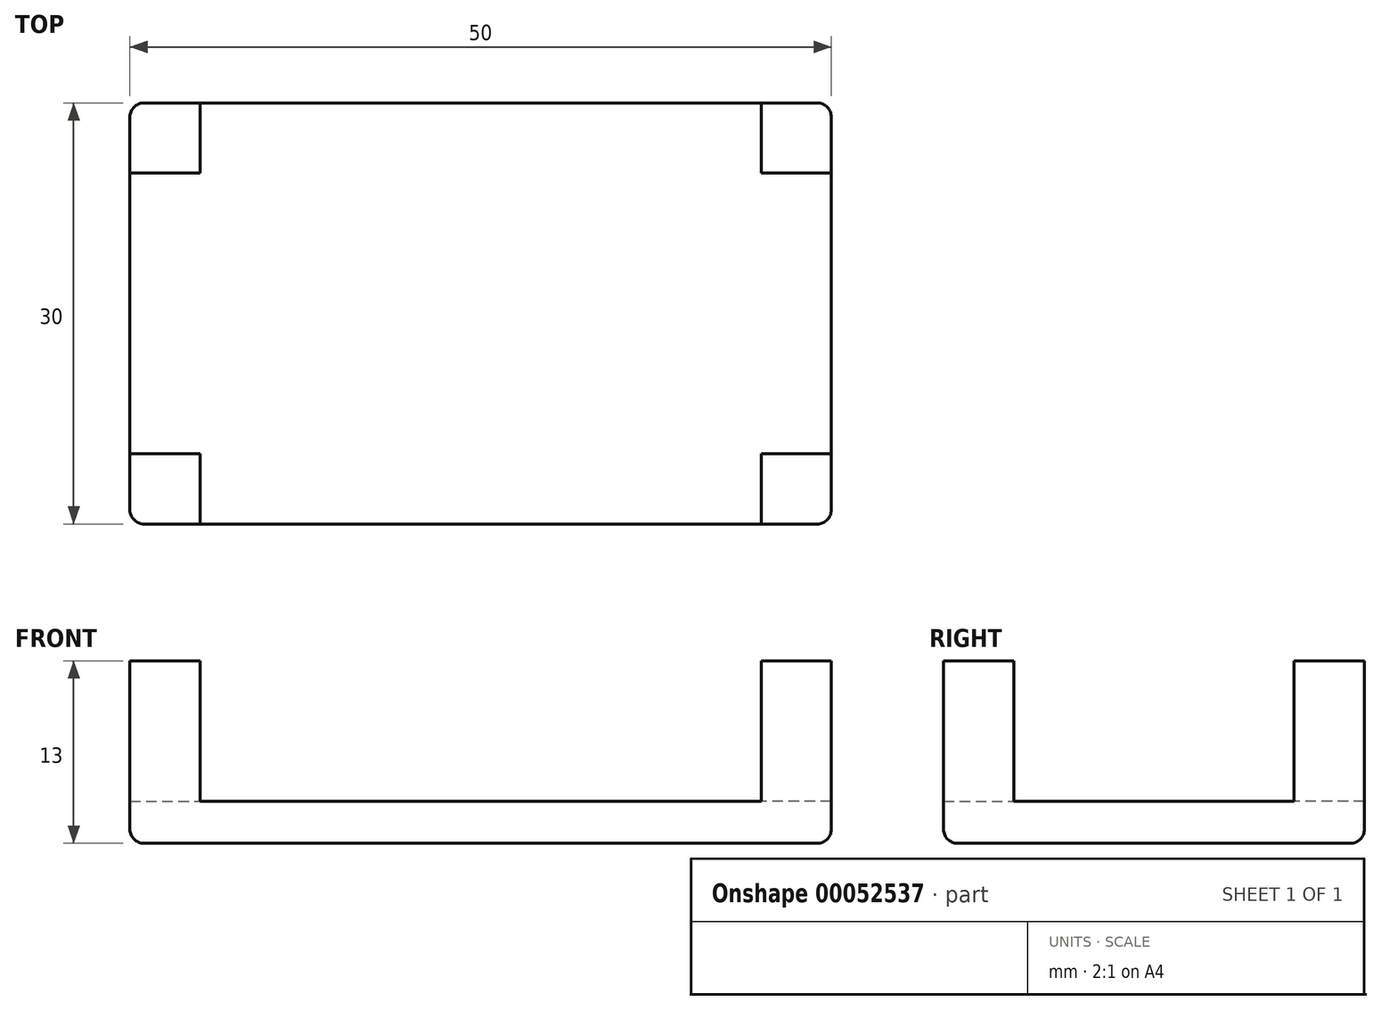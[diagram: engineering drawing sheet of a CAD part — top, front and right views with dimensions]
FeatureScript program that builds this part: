
annotation { "Feature Type Name" : "Feature", "Feature Type Description" : "" }
export const myFeature = defineFeature(function(context is Context, id is Id, definition is map)
    precondition{}
    {
        {
            var Q0;
            Q0=qCreatedBy(makeId("Top.planeOp"),FACE);
            var sketch = newSketch(context, id + "F0", { "sketchPlane" : qUnion([Q0])});
            skLineSegment(sketch, "E0.bottom", {"start": v(-25, 20) * mm, "end": v(25, 20) * mm});
            skLineSegment(sketch, "E0.top", {"start": v(-25, -10) * mm, "end": v(25, -10) * mm});
            skLineSegment(sketch, "E0.left", {"start": v(-25, 20) * mm, "end": v(-25, -10) * mm});
            skLineSegment(sketch, "E0.right", {"start": v(25, 20) * mm, "end": v(25, -10) * mm});
            skSolve(sketch);
        }
        {
            var Q0;
            Q0 = qSketchRegion(id + "F0", true);
            extrude(context, id + "F1", {"entities" : qUnion([Q0]), "depth" : 3 * mm});
        }
        {
            var Q0;
            Q0=makeQuery(id+"F1.opExtrude","CAP_FACE",FACE,{"disambiguationData":[OSD([sQuery(id+"F0.wireOp",EDGE,"E0.bottom"),sQuery(id+"F0.wireOp",EDGE,"E0.top"),sQuery(id+"F0.wireOp",EDGE,"E0.left"),sQuery(id+"F0.wireOp",EDGE,"E0.right")])],"isStart":false});
            var sketch = newSketch(context, id + "F2", { "sketchPlane" : qUnion([Q0])});
            skLineSegment(sketch, "E1.bottom", {"start": v(-25, 20) * mm, "end": v(-20, 20) * mm});
            skLineSegment(sketch, "E1.top", {"start": v(-25, 15) * mm, "end": v(-20, 15) * mm});
            skLineSegment(sketch, "E1.left", {"start": v(-25, 20) * mm, "end": v(-25, 15) * mm});
            skLineSegment(sketch, "E1.right", {"start": v(-20, 20) * mm, "end": v(-20, 15) * mm});
            skLineSegment(sketch, "E2.bottom", {"start": v(-25, -10) * mm, "end": v(-20, -10) * mm});
            skLineSegment(sketch, "E2.top", {"start": v(-25, -5) * mm, "end": v(-20, -5) * mm});
            skLineSegment(sketch, "E2.left", {"start": v(-25, -10) * mm, "end": v(-25, -5) * mm});
            skLineSegment(sketch, "E2.right", {"start": v(-20, -10) * mm, "end": v(-20, -5) * mm});
            skLineSegment(sketch, "E3.bottom", {"start": v(25, 20) * mm, "end": v(20, 20) * mm});
            skLineSegment(sketch, "E3.top", {"start": v(25, 15) * mm, "end": v(20, 15) * mm});
            skLineSegment(sketch, "E3.left", {"start": v(25, 20) * mm, "end": v(25, 15) * mm});
            skLineSegment(sketch, "E3.right", {"start": v(20, 20) * mm, "end": v(20, 15) * mm});
            skLineSegment(sketch, "E4.bottom", {"start": v(25, -10) * mm, "end": v(20, -10) * mm});
            skLineSegment(sketch, "E4.top", {"start": v(25, -5) * mm, "end": v(20, -5) * mm});
            skLineSegment(sketch, "E4.left", {"start": v(25, -10) * mm, "end": v(25, -5) * mm});
            skLineSegment(sketch, "E4.right", {"start": v(20, -10) * mm, "end": v(20, -5) * mm});
            skSolve(sketch);
        }
        {
            var Q0;
            Q0=makeQuery(id+"F2.imprint","IMPRINT",FACE,{"disambiguationData":[TD([[makeQuery(id+"F2.imprint","IMPRINT",EDGE,{"derivedFrom":sQuery(id+"F2.wireOp",EDGE,"E1.bottom")}),-1.0]])]});
            var Q1;
            Q1=makeQuery(id+"F2.imprint","IMPRINT",FACE,{"disambiguationData":[TD([[makeQuery(id+"F2.imprint","IMPRINT",EDGE,{"derivedFrom":sQuery(id+"F2.wireOp",EDGE,"E3.bottom")}),-1.0]])]});
            var Q2;
            Q2=makeQuery(id+"F2.imprint","IMPRINT",FACE,{"disambiguationData":[TD([[makeQuery(id+"F2.imprint","IMPRINT",EDGE,{"derivedFrom":sQuery(id+"F2.wireOp",EDGE,"E4.bottom")}),1.0]])]});
            var Q3;
            Q3=makeQuery(id+"F2.imprint","IMPRINT",FACE,{"disambiguationData":[TD([[makeQuery(id+"F2.imprint","IMPRINT",EDGE,{"derivedFrom":sQuery(id+"F2.wireOp",EDGE,"E2.bottom")}),1.0]])]});
            extrude(context, id + "F3", {"entities" : qUnion([Q0, Q1, Q2, Q3]), "operationType" : NewBodyOperationType.ADD, "depth" : 10 * mm});
        }
        {
            var Q0;
            Q0=makeQuery(id+"F1.opExtrude","CAP_EDGE",EDGE,{"disambiguationData":[OSD([sQuery(id+"F0.wireOp",EDGE,"E0.bottom")])],"isStart":true});
            fillet(context, id + "F4", {"entities" : qUnion([Q0]), "radius" : 1 * mm, "tangentPropagation" : true, "allowEdgeOverflow" : false});
        }
        {
            var Q0;
            Q0=makeQuery(id+"F1.opExtrude","CAP_EDGE",EDGE,{"disambiguationData":[OSD([sQuery(id+"F0.wireOp",EDGE,"E0.right")])],"isStart":true});
            fillet(context, id + "F5", {"entities" : qUnion([Q0]), "radius" : 1 * mm, "tangentPropagation" : true, "allowEdgeOverflow" : false});
        }
        {
            var Q0;
            Q0=makeQuery(id+"F1.opExtrude","CAP_EDGE",EDGE,{"disambiguationData":[OSD([sQuery(id+"F0.wireOp",EDGE,"E0.top")])],"isStart":true});
            fillet(context, id + "F6", {"entities" : qUnion([Q0]), "radius" : 1 * mm, "tangentPropagation" : true, "allowEdgeOverflow" : false});
        }
        {
            var Q0;
            Q0=makeQuery(id+"F1.opExtrude","CAP_EDGE",EDGE,{"disambiguationData":[OSD([sQuery(id+"F0.wireOp",EDGE,"E0.left")])],"isStart":true});
            fillet(context, id + "F7", {"entities" : qUnion([Q0]), "radius" : 1 * mm, "tangentPropagation" : true, "allowEdgeOverflow" : false});
        }
    });
